# Revit family: Furniture_Office-Chairs_Flokk_Giroflex-68_Mesh
name_source: partatom
category: Furniture
units: mm (PartAtom-declared; Revit-internal decimal feet)

## family parameters
Always vertical = Yes
Cut with Voids When Loaded = No
OmniClass Number = 23.40.20.14.14.11
OmniClass Title = Chairs
Room Calculation Point = No
Shared = No
Work Plane-Based = No

## types (1)
- Giroflex 68 Mesh
    AssetType = Movable
    BIMObjectName = Furniture_Office-Chairs_Flokk_Giroflex-68_Mesh
    Brand = Flokk
    Category = Giroflex
    Color = Various
    Cost = 0 $
    Default Elevation = 0 mm  [stored 0 ft]
    Description = This office chair embodies rationality and industrialization in conjunction with the need for one's own, personal sphere. On the basis of the same substructure, the swivel chairs can be expanded to numerous comfortable variations.
    Designer = Paolo Fancelli
    DurationUnit = Year
    Finish = This version is delivered with a comfortable upholstered backrest.
    HighestSeatingHeight = 500 mm  [stored 1.64042 ft]
    IfcExportAs = IfcFurnishingElementType
    IfcExportType = CHAIR
    LowestSeatingHeight = 500 mm  [stored 1.64042 ft]
    MainColor = Various
    Manufacturer = Flokk
    ManufacturerName = Flokk
    ManufacturerURL = https://www.flokk.com
    Material = Plastic, Metal and Textile
    Model = Giroflex 68 Mesh
    ModelNumber = 68-3519
    NBSDescription = Stacking chairs
    NBSReference = 45-35-20/355
    Name = Giroflex-68_Mesh
    NominalDepth = 683 mm
    NominalHeight = 1099 mm
    NominalLength = 697 mm
    OfficeChairQuaternaryMaterial = Black RAL 9005
    ProductDatasheet = https://flokkplatformprod.blob.core.windows.net
    ProductInformation = This office chair embodies rationality and industrialization in conjunction with the need for one's own, personal sphere. On the basis of the same substructure, the swivel chairs can be expanded to numerous comfortable variations.
    SeatingHeight = 500 mm  [stored 1.64042 ft]
    Shape = Sculptured
    Size = 700x685x1100 mm
    URL = https://store.flokk.com
    Uniclass2 = Pr_40_50_12_51
    Uniclass2015Description = Meeting room chairs
    Uniclass2015Reference = Pr_40_50_12_51
    Version = 1
    VersionDate = 16/12/2022
    WarrantyDurationUnit = Year

note: [stored X ft] marks values corroborated as IEEE doubles in the binary element streams (Revit-internal decimal feet)

## geometry (parser evidence)
native form markers: Sweep x3
no freeform markers — native parametric forms only
